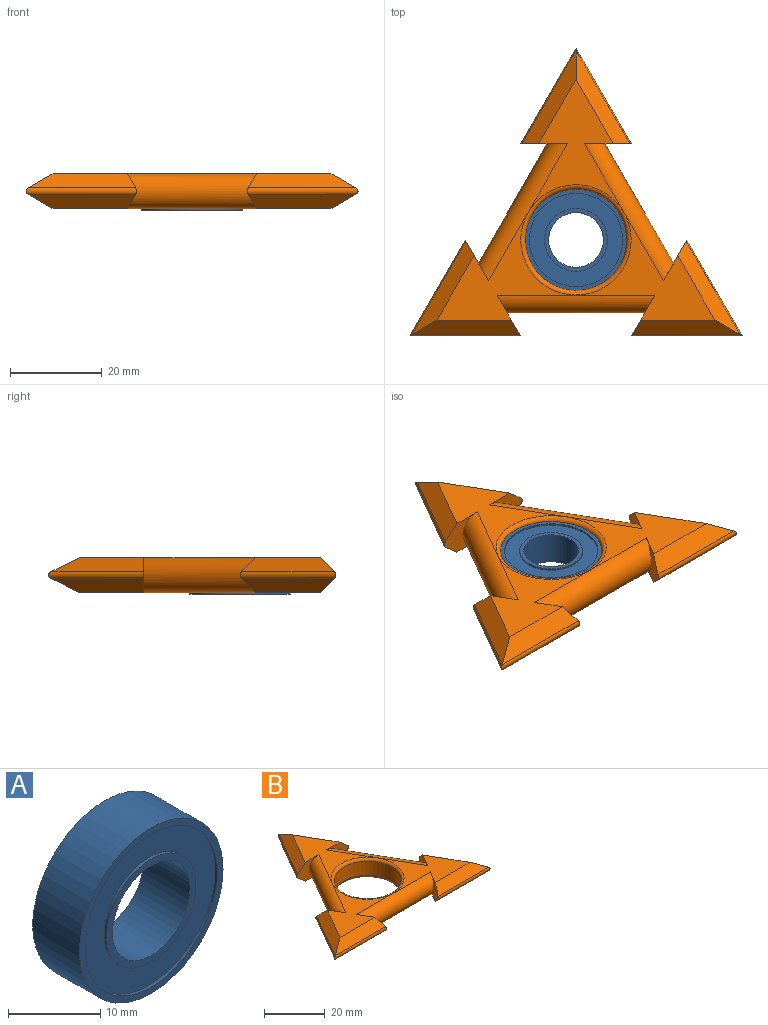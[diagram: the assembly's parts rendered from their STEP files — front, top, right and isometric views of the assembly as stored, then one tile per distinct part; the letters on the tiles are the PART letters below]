
ASSEMBLY  parts=2 mates=1
PART A: 12 faces, bbox 22x7.2x22 mm
  f0: plane 13.72x13.72mm, normal (0,1,0), area 35.8mm2, adj f2,f9
  f1: plane 13.72x13.72mm, normal (0,-1,0), area 35.8mm2, adj f2,f6
  f2: cylinder r=5.97mm len=11.94mm, axis (0,1,0), area 268.6mm2, adj f0,f1
  f3: cylinder r=11.01mm len=22.02mm, axis (0,1,0), area 495.5mm2, adj f4,f5
  f4: plane 22.02x22.02mm, normal (0,-1,0), area 56.6mm2, adj f3,f7
  f5: plane 22.02x22.02mm, normal (0,1,0), area 56.6mm2, adj f3,f10
  f6: cylinder r=6.86mm len=13.72mm, axis (0,-1,0), area 16.4mm2, adj f1,f8
  f7: cylinder r=10.16mm len=20.32mm, axis (0,-1,0), area 24.3mm2, adj f4,f8
  f8: plane 20.32x20.32mm, normal (0,-1,0), area 176.5mm2, adj f6,f7
  f9: cylinder r=6.86mm len=13.72mm, axis (0,1,0), area 16.4mm2, adj f0,f11
  f10: cylinder r=10.16mm len=20.32mm, axis (0,1,0), area 24.3mm2, adj f5,f11
  f11: plane 20.32x20.32mm, normal (0,1,0), area 176.5mm2, adj f9,f10
PART B: 32 faces, bbox 72.3x62.8x7.6 mm
  f0: plane 8.81x7.62mm, normal (-0.87,0.5,0), area 37.8mm2, adj f7,f8,f14,f16,f21,f28
  f1: plane 8.81x7.62mm, normal (-0.87,0.5,0), area 37.8mm2, adj f7,f8,f13,f15,f22,f29
  f2: plane 10.17x7.62mm, normal (0,-1,0), area 37.8mm2, adj f7,f8,f10,f12,f22,f30
  f3: plane 10.17x7.62mm, normal (0,-1,0), area 37.8mm2, adj f7,f8,f9,f11,f23,f31
  f4: plane 8.81x7.62mm, normal (0.87,0.5,0), area 37.8mm2, adj f7,f8,f18,f20,f23,f26
  f5: plane 8.81x7.62mm, normal (0.87,0.5,0), area 37.8mm2, adj f7,f8,f17,f19,f21,f27
  f6: cylinder r=11.02mm len=22.04mm, axis (0,0,-1), area 389.1mm2, adj f24,f25
  f7: plane 60.55x52.44mm, normal (0,0,1), area 626mm2, adj f0,f1,f2,f3,f4,f5,f9,f10
  f8: plane 60.55x52.44mm, normal (0,0,-1), area 626mm2, adj f0,f1,f2,f3,f4,f5,f11,f12
  f9: plane 20.24x11.68mm, normal (-0.61,0.35,0.71), area 86.8mm2, adj f3,f7,f10,f31
  f10: plane 20.24x11.68mm, normal (0.61,0.35,0.71), area 86.8mm2, adj f2,f7,f9,f30
  f11: plane 20.24x11.68mm, normal (-0.61,0.35,-0.71), area 86.8mm2, adj f3,f8,f12,f31
  f12: plane 20.24x11.68mm, normal (0.61,0.35,-0.71), area 86.8mm2, adj f2,f8,f11,f30
  f13: plane 20.24x13.48mm, normal (0.61,0.35,0.71), area 86.8mm2, adj f1,f7,f14,f29
  f14: plane 23.37x3.1mm, normal (0,-0.71,0.71), area 86.8mm2, adj f0,f7,f13,f28
  f15: plane 20.24x13.48mm, normal (0.61,0.35,-0.71), area 86.8mm2, adj f1,f8,f16,f29
  f16: plane 23.37x3.1mm, normal (0,-0.71,-0.71), area 86.8mm2, adj f0,f8,f15,f28
  f17: plane 23.37x3.1mm, normal (0,-0.71,0.71), area 86.8mm2, adj f5,f7,f18,f27
  f18: plane 20.24x13.48mm, normal (-0.61,0.35,0.71), area 86.8mm2, adj f4,f7,f17,f26
  f19: plane 23.37x3.1mm, normal (0,-0.71,-0.71), area 86.8mm2, adj f5,f8,f20,f27
  f20: plane 20.24x13.48mm, normal (-0.61,0.35,-0.71), area 86.8mm2, adj f4,f8,f19,f26
  f21: cylinder r=3.81mm len=34.4mm, axis (-1,0,0), area 378.2mm2, adj f0,f5,f7,f8
  f22: cylinder r=3.81mm len=31.7mm, axis (0.5,-0.87,0), area 378.2mm2, adj f1,f2,f7,f8
  f23: cylinder r=3.81mm len=31.7mm, axis (0.5,0.87,0), area 378.2mm2, adj f3,f4,f7,f8
  f24: torus R=12.02mm, axis (0,0,1), area 112.3mm2, adj f6,f8
  f25: torus R=12.02mm, axis (0,0,1), area 112.3mm2, adj f6,f7
  f26: cylinder r=1mm len=20.97mm, axis (-0.5,-0.87,0), area 37.4mm2, adj f4,f18,f20,f27
  f27: cylinder r=1mm len=24.05mm, axis (1,0,0), area 37.4mm2, adj f5,f17,f19,f26
  f28: cylinder r=1mm len=24.05mm, axis (1,0,0), area 37.4mm2, adj f0,f14,f16,f29
  f29: cylinder r=1mm len=20.97mm, axis (-0.5,0.87,0), area 37.4mm2, adj f1,f13,f15,f28
  f30: cylinder r=1mm len=20.97mm, axis (-0.5,0.87,0), area 37.4mm2, adj f2,f10,f12,f31
  f31: cylinder r=1mm len=20.97mm, axis (-0.5,-0.87,0), area 37.4mm2, adj f3,f9,f11,f30
PLACE A rot(axis=(0.58,0.58,0.58),120deg) t=(0,0,3.2)mm
PLACE B at identity
MATE fastened A.f2 <-> B.f6  axis (0,0,-1) through (0,0,0)mm
